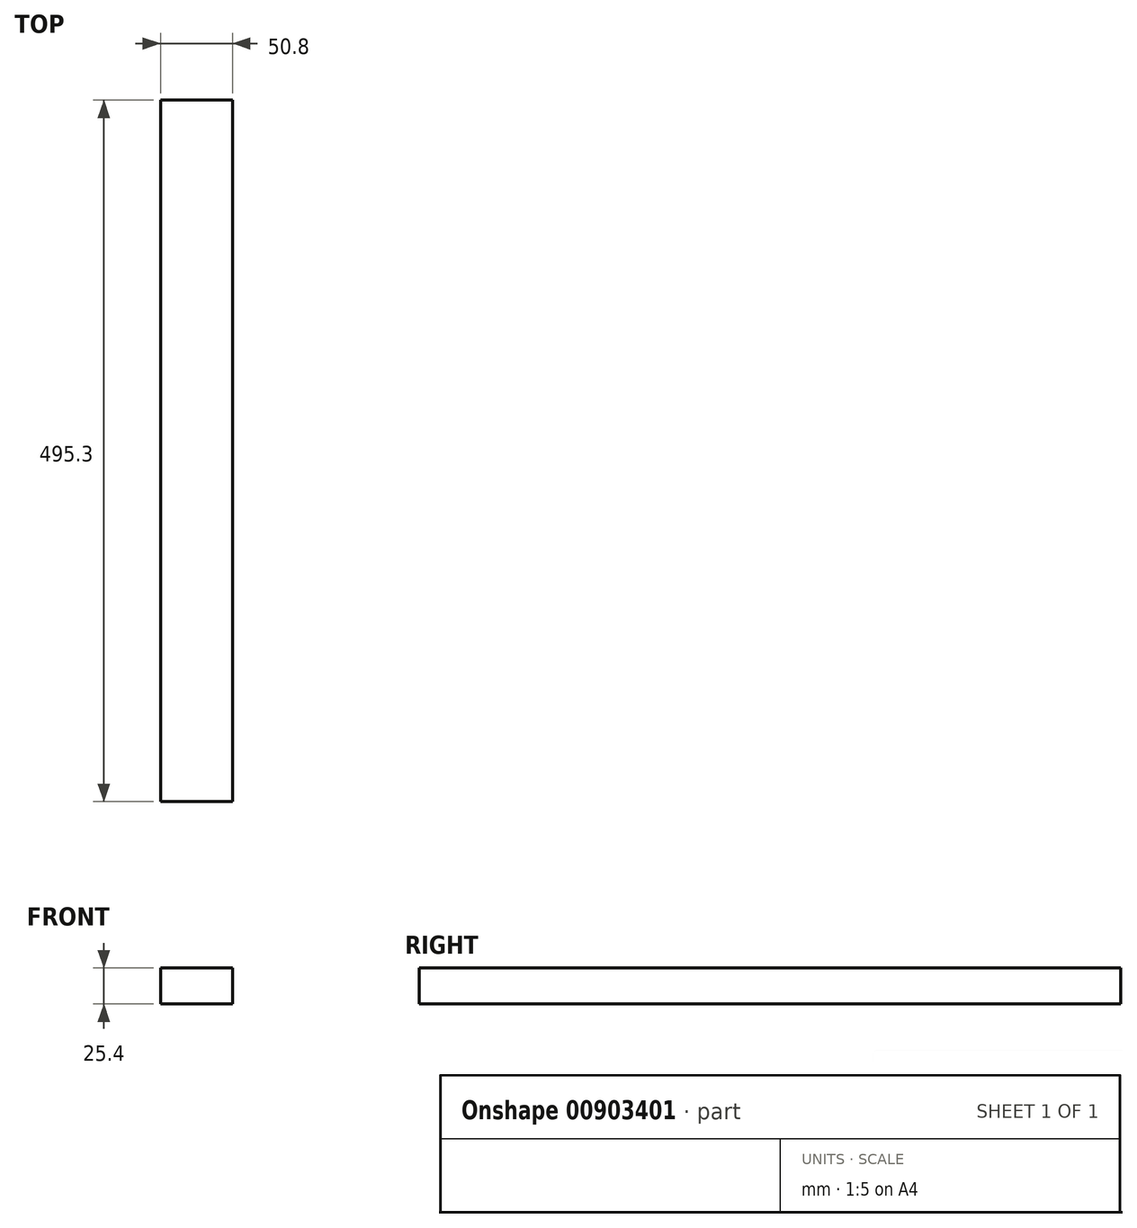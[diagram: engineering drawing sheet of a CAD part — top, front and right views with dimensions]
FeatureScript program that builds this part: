
annotation { "Feature Type Name" : "Feature", "Feature Type Description" : "" }
export const myFeature = defineFeature(function(context is Context, id is Id, definition is map)
    precondition{}
    {
        {
            var Q0;
            Q0=qCreatedBy(makeId("Front.planeOp"),FACE);
            var sketch = newSketch(context, id + "F0", { "sketchPlane" : qUnion([Q0])});
            skLineSegment(sketch, "E0.bottom", {"start": v(0, 0) * mm, "end": v(50.8, 0) * mm});
            skLineSegment(sketch, "E0.top", {"start": v(0, 25.4) * mm, "end": v(50.8, 25.4) * mm});
            skLineSegment(sketch, "E0.left", {"start": v(0, 0) * mm, "end": v(0, 25.4) * mm});
            skLineSegment(sketch, "E0.right", {"start": v(50.8, 0) * mm, "end": v(50.8, 25.4) * mm});
            skSolve(sketch);
        }
        {
            var Q0;
            Q0=makeQuery(id+"F0.imprint","IMPRINT",FACE,{"disambiguationData":[TD([[makeQuery(id+"F0.imprint","IMPRINT",EDGE,{"derivedFrom":sQuery(id+"F0.wireOp",EDGE,"E0.bottom")}),1.0]])]});
            extrude(context, id + "F1", {"entities" : qUnion([Q0]), "depth" : 495.3 * mm, "offsetDistance" : 25.4 * mm});
        }
    });
